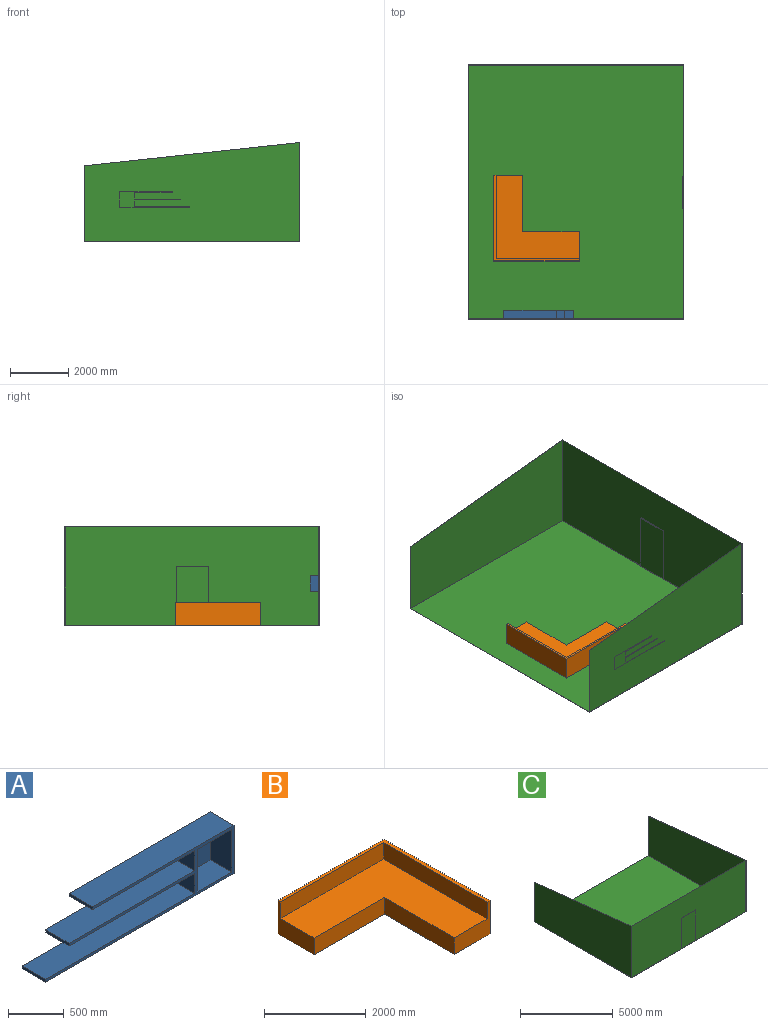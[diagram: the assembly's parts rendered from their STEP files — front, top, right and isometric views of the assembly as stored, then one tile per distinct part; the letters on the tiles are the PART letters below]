
ASSEMBLY  parts=3 mates=2
PART A: 19 faces, bbox 2400x300x530 mm
  f0: plane 2400x530mm, normal (0,-1,0), area 202200mm2, adj f2,f3,f4,f5,f6,f7,f9,f10
  f1: plane 2400x530mm, normal (0,1,0), area 409000mm2, adj f2,f3,f4,f5,f6,f7,f13,f14
  f2: plane 1900x300mm, normal (0,0,1), area 570000mm2, adj f0,f1,f4,f18
  f3: plane 2400x300mm, normal (0,0,-1), area 720000mm2, adj f0,f1,f7,f18
  f4: plane 300x220mm, normal (-1,0,0), area 66000mm2, adj f0,f1,f2,f16
  f5: plane 300x220mm, normal (-1,0,0), area 66000mm2, adj f0,f1,f14,f15
  f6: plane 1800x300mm, normal (0,0,1), area 540000mm2, adj f0,f1,f7,f13
  f7: plane 530x300mm, normal (1,0,0), area 159000mm2, adj f0,f1,f3,f6
  f8: plane 470x440mm, normal (0,-1,0), area 206800mm2, adj f9,f10,f11,f12
  f9: plane 440x270mm, normal (0,0,-1), area 118800mm2, adj f0,f8,f10,f11
  f10: plane 470x270mm, normal (-1,0,0), area 126900mm2, adj f0,f8,f9,f12
  f11: plane 470x270mm, normal (1,0,0), area 126900mm2, adj f0,f8,f9,f12
  f12: plane 440x270mm, normal (0,0,1), area 118800mm2, adj f0,f8,f10,f11
  f13: plane 300x30mm, normal (-1,0,0), area 9000mm2, adj f0,f1,f6,f14
  f14: plane 1300x300mm, normal (0,0,-1), area 390000mm2, adj f0,f1,f5,f13
  f15: plane 1600x300mm, normal (0,0,1), area 480000mm2, adj f0,f1,f5,f17
  f16: plane 1600x300mm, normal (0,0,-1), area 480000mm2, adj f0,f1,f4,f17
  f17: plane 300x30mm, normal (-1,0,0), area 9000mm2, adj f0,f1,f15,f16
  f18: plane 300x30mm, normal (-1,0,0), area 9000mm2, adj f0,f1,f2,f3
PART B: 11 faces, bbox 2940x2940x800 mm
  f0: plane 2940x800mm, normal (1,0,0), area 2352000mm2, adj f1,f5,f7,f10
  f1: plane 2940x800mm, normal (0,1,0), area 2352000mm2, adj f0,f2,f5,f10
  f2: plane 1000x800mm, normal (-1,0,0), area 427380mm2, adj f1,f3,f4,f5,f8,f10
  f3: plane 1950x400mm, normal (0,-1,0), area 780000mm2, adj f2,f4,f5,f6
  f4: plane 2871.55x2858.28mm, normal (0,0,1), area 4424697.9mm2, adj f2,f3,f6,f7,f8,f9
  f5: plane 2940x2940mm, normal (0,0,-1), area 4860600mm2, adj f0,f1,f2,f3,f6,f7
  f6: plane 1940x400mm, normal (-1,0,0), area 776000mm2, adj f3,f4,f5,f7
  f7: plane 990x800mm, normal (0,-1,0), area 428687.4mm2, adj f0,f4,f5,f6,f9,f10
  f8: plane 2858.28x400mm, normal (0,-1,0), area 1143312.6mm2, adj f2,f4,f9,f10
  f9: plane 2871.55x400mm, normal (-1,0,0), area 1148620mm2, adj f4,f7,f8,f10
  f10: plane 2940x2940mm, normal (0,0,1), area 435902.1mm2, adj f0,f1,f2,f7,f8,f9
PART C: 18 faces, bbox 8730x7400x3400 mm
  f0: plane 8700x7399mm, normal (0,0,1), area 64344900mm2, adj f1,f3,f6,f11,f15,f16,f17
  f1: plane 8700x3390mm, normal (0,1,0), area 27271913.5mm2, adj f0,f2,f3,f9,f10,f11,f14,f15
  f2: plane 1x0.11mm, normal (-1,0,0), area 0.1mm2, adj f1,f10,f12
  f3: plane 7399x3389.89mm, normal (-1,0,0), area 22122610.1mm2, adj f0,f1,f6,f7
  f4: plane 8730x3400mm, normal (0,-1,0), area 29682000mm2, adj f5,f7,f8,f10,f12,f13
  f5: plane 8730x7400mm, normal (0,0,-1), area 64602000mm2, adj f4,f6,f8,f13
  f6: plane 8730x2600mm, normal (0,1,0), area 165000mm2, adj f0,f3,f5,f7,f8,f11,f12,f13
  f7: plane 7400x800mm, normal (0,0.11,0.99), area 186077.9mm2, adj f3,f4,f6,f8,f9
  f8: plane 7400x3400mm, normal (1,0,0), area 22200000mm2, adj f4,f5,f6,f7
  f9: plane 1x0.11mm, normal (1,0,0), area 0.1mm2, adj f1,f7,f10
  f10: plane 8700x1mm, normal (0,0,1), area 8700mm2, adj f1,f2,f4,f9
  f11: plane 7399x3389.89mm, normal (1,0,0), area 22122610.1mm2, adj f0,f1,f6,f12
  f12: plane 7400x800mm, normal (0,0.11,0.99), area 37215.6mm2, adj f2,f4,f6,f11,f13
  f13: plane 7400x3400mm, normal (-1,0,0), area 22200000mm2, adj f4,f5,f6,f12
  f14: plane 1100x24mm, normal (0,0,1), area 26400mm2, adj f1,f15,f16,f17
  f15: plane 2019.17x24mm, normal (1,0,0), area 48460.1mm2, adj f0,f1,f14,f17
  f16: plane 2019.17x24mm, normal (-1,0,0), area 48460.1mm2, adj f0,f1,f14,f17
  f17: plane 2019.17x1100mm, normal (0,1,0), area 2221086.5mm2, adj f0,f14,f15,f16
PLACE A rot(axis=(0,0,1),180deg) t=(-2181.33,-4476.54,1667.32)mm
PLACE B rot(axis=(0,0,1),180deg) t=(-3681.73,-2634.96,-10)mm
PLACE C rot(axis=(0,0,1),90deg) t=(-852.97,-276.54,-10)mm
MATE planar C.f11 <-> A.f1  axis (0,1,0) through (-688.51,-4626.54,1503.89)mm
MATE planar C.f5 <-> B.f5  axis (0,0,-1) through (-4552.97,-266.54,-10)mm
